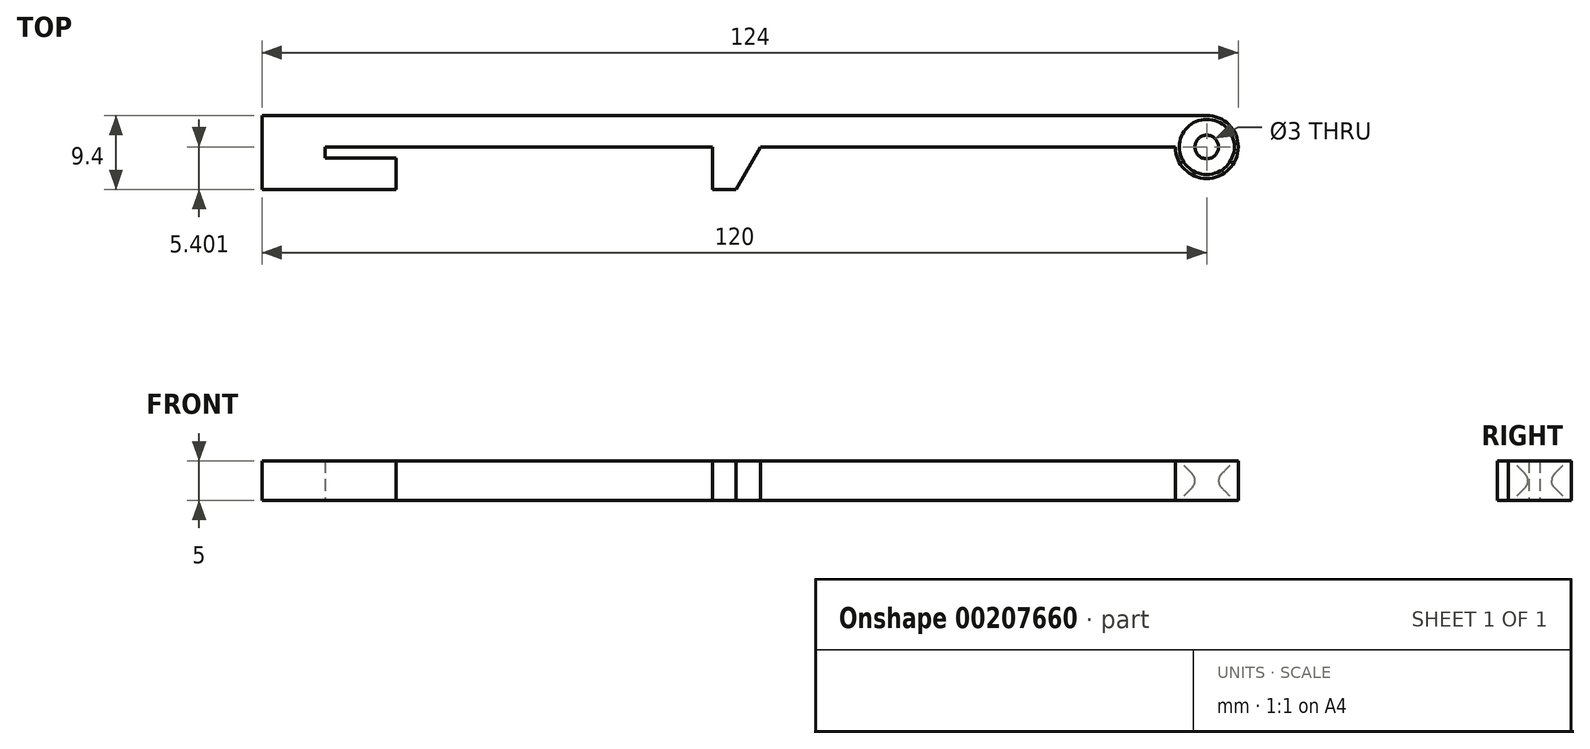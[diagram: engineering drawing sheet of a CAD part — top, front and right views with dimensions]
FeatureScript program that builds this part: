
annotation { "Feature Type Name" : "Feature", "Feature Type Description" : "" }
export const myFeature = defineFeature(function(context is Context, id is Id, definition is map)
    precondition{}
    {
        {
            var Q0;
            Q0=qCreatedBy(makeId("Top.planeOp"),FACE);
            var sketch = newSketch(context, id + "F0", { "sketchPlane" : qUnion([Q0])});
            skLineSegment(sketch, "E0", {"start": v(-103, 1.6) * mm, "end": v(-120, 1.6) * mm});
            skLineSegment(sketch, "E1", {"start": v(-120, 1.6) * mm, "end": v(-120, 11) * mm});
            skLineSegment(sketch, "E2", {"start": v(-120, 11) * mm, "end": v(0, 11) * mm});
            skLineSegment(sketch, "E3", {"start": v(-103, 1.6) * mm, "end": v(-103, 5.6) * mm});
            skLineSegment(sketch, "E4", {"start": v(-103, 5.6) * mm, "end": v(-112, 5.6) * mm});
            skLineSegment(sketch, "E5", {"start": v(-112, 5.6) * mm, "end": v(-112, 7) * mm});
            skLineSegment(sketch, "E6", {"start": v(-112, 7) * mm, "end": v(-62.8, 7) * mm});
            skLineSegment(sketch, "E7", {"start": v(0, 11) * mm, "end": v(0, 7) * mm});
            skCircle(sketch, "E8", {"center": v(0, 7) * mm, "radius": 4 * mm});
            skCircle(sketch, "E9", {"center": v(0, 7) * mm, "radius": 1.5 * mm});
            skLineSegment(sketch, "E10", {"start": v(-62.8, 7) * mm, "end": v(-62.8, 1.6) * mm});
            skLineSegment(sketch, "E11", {"start": v(-62.8, 1.6) * mm, "end": v(-59.8, 1.6) * mm});
            skLineSegment(sketch, "E12", {"start": v(-59.8, 1.6) * mm, "end": v(-56.68, 7) * mm});
            skLineSegment(sketch, "E13.trimOffspring", {"start": v(-56.68, 7) * mm, "end": v(0, 7) * mm});
            skSolve(sketch);
        }
        {
            var Q0;
            Q0 = qSketchRegion(id + "F0", true);
            extrude(context, id + "F1", {"entities" : qUnion([Q0]), "depth" : 5 * mm});
        }
        {
            var Q0;
            Q0=makeQuery(id+"F1.opExtrude","CAP_EDGE",EDGE,{"disambiguationData":[OSD([sQuery(id+"F0.wireOp",EDGE,"E9")])],"isStart":false});
            var Q1;
            Q1=makeQuery(id+"F1.opExtrude","CAP_EDGE",EDGE,{"disambiguationData":[OSD([sQuery(id+"F0.wireOp",EDGE,"E9")])],"isStart":true});
            chamfer(context, id + "F2", {"entities" : qUnion([Q0, Q1]), "width" : 2 * mm});
        }
        {
            var Q0;
            Q0=makeQuery(id+"F1.opExtrude","SWEPT_FACE",FACE,{"disambiguationData":[OSD([sQuery(id+"F0.wireOp",EDGE,"E9")])]});
            fillet(context, id + "F3", {"entities" : qUnion([Q0]), "radius" : 1.2 * mm, "tangentPropagation" : true, "allowEdgeOverflow" : false});
        }
    });
